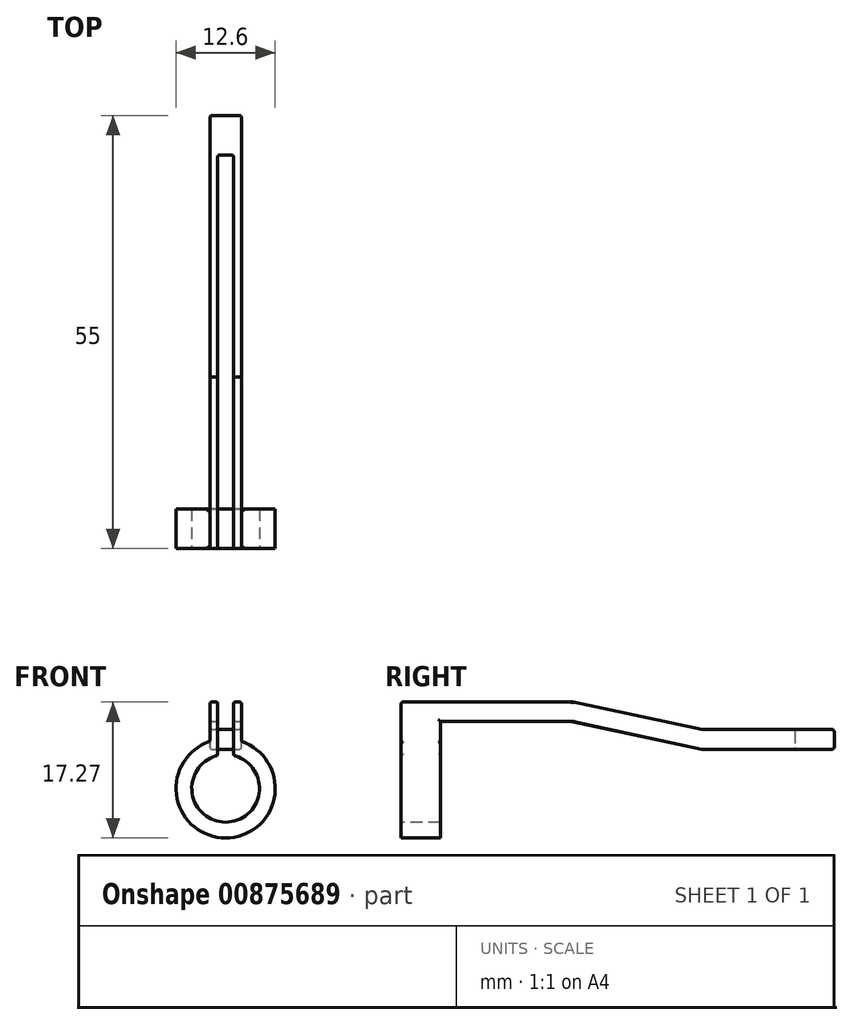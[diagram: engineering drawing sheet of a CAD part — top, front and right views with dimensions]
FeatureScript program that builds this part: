
annotation { "Feature Type Name" : "Feature", "Feature Type Description" : "" }
export const myFeature = defineFeature(function(context is Context, id is Id, definition is map)
    precondition{}
    {
        {
            var Q0;
            Q0=qCreatedBy(makeId("Front.planeOp"),FACE);
            var sketch = newSketch(context, id + "F0", { "sketchPlane" : qUnion([Q0])});
            skCircle(sketch, "E0", {"center": v(0, 0) * mm, "radius": 6.3 * mm});
            skSolve(sketch);
        }
        {
            var Q0;
            Q0 = qSketchRegion(id + "F0", true);
            extrude(context, id + "F1", {"entities" : qUnion([Q0]), "depth" : 5 * mm, "offsetDistance" : 25 * mm});
        }
        {
            var Q0;
            Q0=makeQuery(id+"F1.opExtrude","CAP_FACE",FACE,{"disambiguationData":[OSD([sQuery(id+"F0.wireOp",EDGE,"E0")])],"isStart":false});
            var sketch = newSketch(context, id + "F2", { "sketchPlane" : qUnion([Q0])});
            skCircle(sketch, "E1", {"center": v(0, 0) * mm, "radius": 4.3 * mm});
            skSolve(sketch);
        }
        {
            var Q0;
            Q0=makeQuery(id+"F2.imprint","IMPRINT",FACE,{"disambiguationData":[TD([[makeQuery(id+"F2.imprint","IMPRINT",EDGE,{"derivedFrom":sQuery(id+"F2.wireOp",EDGE,"E1")}),1.0]])]});
            extrude(context, id + "F3", {"entities" : qUnion([Q0]), "operationType" : NewBodyOperationType.REMOVE, "endBound" : BoundingType.UP_TO_NEXT, "oppositeDirection" : true, "depth" : 25 * mm, "offsetDistance" : 25 * mm});
        }
        {
            var Q0;
            Q0=makeQuery(id+"F1.opExtrude","CAP_FACE",FACE,{"disambiguationData":[OSD([sQuery(id+"F0.wireOp",EDGE,"E0")])],"isStart":false});
            var sketch = newSketch(context, id + "F4", { "sketchPlane" : qUnion([Q0])});
            skLineSegment(sketch, "E2.bottom", {"start": v(2, 5.97) * mm, "end": v(-2, 5.97) * mm});
            skLineSegment(sketch, "E2.top", {"start": v(2, 10.97) * mm, "end": v(-2, 10.97) * mm});
            skLineSegment(sketch, "E2.left", {"start": v(2, 5.97) * mm, "end": v(2, 10.97) * mm});
            skLineSegment(sketch, "E2.right", {"start": v(-2, 5.97) * mm, "end": v(-2, 10.97) * mm});
            skPoint(sketch, "E2.middle", {"position": v(0, 8.47) * mm});
            skSolve(sketch);
        }
        {
            var Q0;
            Q0 = qSketchRegion(id + "F4", true);
            extrude(context, id + "F5", {"entities" : qUnion([Q0]), "operationType" : NewBodyOperationType.ADD, "oppositeDirection" : true, "depth" : 5 * mm, "offsetDistance" : 25 * mm});
        }
        {
            var Q0;
            Q0=makeQuery(id+"F5.opExtrude","SWEPT_FACE",FACE,{"disambiguationData":[OSD([sQuery(id+"F4.wireOp",EDGE,"E2.left")])]});
            var sketch = newSketch(context, id + "F6", { "sketchPlane" : qUnion([Q0])});
            skLineSegment(sketch, "E3", {"start": v(0, 10.97) * mm, "end": v(16.79, 10.97) * mm});
            skLineSegment(sketch, "E4", {"start": v(33.21, 7.47) * mm, "end": v(16.79, 10.97) * mm});
            skLineSegment(sketch, "E5", {"start": v(50, 7.47) * mm, "end": v(33.21, 7.47) * mm});
            skLineSegment(sketch, "E6", {"start": v(50, 7.47) * mm, "end": v(50, 4.97) * mm});
            skLineSegment(sketch, "E7", {"start": v(50, 4.97) * mm, "end": v(33.21, 4.97) * mm});
            skLineSegment(sketch, "E8", {"start": v(33.21, 4.97) * mm, "end": v(16.79, 8.47) * mm});
            skLineSegment(sketch, "E9", {"start": v(16.79, 8.47) * mm, "end": v(0, 8.47) * mm});
            skSolve(sketch);
        }
        {
            var Q0;
            {var subQ0=sQuery(id+"F6.wireOp",EDGE,"E3");Q0=makeQuery(id+"F6.imprint","IMPRINT",FACE,{"disambiguationData":[TD([[makeQuery(id+"F6.imprint","IMPRINT",EDGE,{"derivedFrom":subQ0}),-1.0]])]});}
            var Q1;
            Q1=makeQuery(id+"F5.opExtrude","SWEPT_FACE",FACE,{"disambiguationData":[OSD([sQuery(id+"F4.wireOp",EDGE,"E2.right")])]});
            extrude(context, id + "F7", {"entities" : qUnion([Q0]), "operationType" : NewBodyOperationType.ADD, "endBound" : BoundingType.UP_TO_SURFACE, "oppositeDirection" : true, "depth" : 25 * mm, "endBoundEntityFace" : qUnion([Q1]), "offsetDistance" : 25 * mm});
        }
        {
            var Q0;
            Q0=makeQuery(id+"F5.boolean.opBoolean","MERGE",FACE,{"derivedFrom":[makeQuery(id+"F1.opExtrude","CAP_FACE",FACE,{"disambiguationData":[OSD([sQuery(id+"F0.wireOp",EDGE,"E0")])],"isStart":false}),makeQuery(id+"F5.opExtrude","CAP_FACE",FACE,{"disambiguationData":[OSD([sQuery(id+"F4.wireOp",EDGE,"E2.bottom"),sQuery(id+"F4.wireOp",EDGE,"E2.top"),sQuery(id+"F4.wireOp",EDGE,"E2.left"),sQuery(id+"F4.wireOp",EDGE,"E2.right")])],"isStart":true})]});
            var sketch = newSketch(context, id + "F8", { "sketchPlane" : qUnion([Q0])});
            skLineSegment(sketch, "E10.bottom", {"start": v(1, 10.97) * mm, "end": v(-1, 10.97) * mm});
            skLineSegment(sketch, "E10.top", {"start": v(1, 2.97) * mm, "end": v(-1, 2.97) * mm});
            skLineSegment(sketch, "E10.left", {"start": v(1, 10.97) * mm, "end": v(1, 2.97) * mm});
            skLineSegment(sketch, "E10.right", {"start": v(-1, 10.97) * mm, "end": v(-1, 2.97) * mm});
            skPoint(sketch, "E11", {"position": v(0, 2.97) * mm});
            skSolve(sketch);
        }
        {
            var Q0;
            {var subQ0=sQuery(id+"F8.wireOp",EDGE,"E10.bottom");Q0=makeQuery(id+"F8.imprint","IMPRINT",FACE,{"disambiguationData":[TD([[makeQuery(id+"F8.imprint","IMPRINT",EDGE,{"derivedFrom":subQ0}),1.0]])]});}
            var Q1;
            Q1=sQuery(id+"F8.wireOp",EDGE,"E10.right");
            extrude(context, id + "F9", {"entities" : qUnion([Q0]), "operationType" : NewBodyOperationType.REMOVE, "surfaceEntities" : qUnion([Q1]), "oppositeDirection" : true, "depth" : 50 * mm, "offsetDistance" : 25 * mm});
        }
        {
            var Q0;
            Q0=makeQuery(id+"F7.opExtrude","CAP_EDGE",EDGE,{"disambiguationData":[OSD([sQuery(id+"F6.wireOp",EDGE,"E9")])],"isStart":false});
            var Q1;
            Q1=makeQuery(id+"F5.opExtrude","CAP_EDGE",EDGE,{"disambiguationData":[OSD([sQuery(id+"F4.wireOp",EDGE,"E2.right")])],"isStart":false});
            var Q2;
            Q2=makeQuery(id+"F9.boolean.opBoolean","INTERSECT",EDGE,{"derivedFrom":[makeQuery(id+"F5.boolean.opBoolean","MERGE",FACE,{"derivedFrom":[makeQuery(id+"F1.opExtrude","CAP_FACE",FACE,{"disambiguationData":[OSD([sQuery(id+"F0.wireOp",EDGE,"E0")])],"isStart":true}),makeQuery(id+"F5.opExtrude","CAP_FACE",FACE,{"disambiguationData":[OSD([sQuery(id+"F4.wireOp",EDGE,"E2.bottom"),sQuery(id+"F4.wireOp",EDGE,"E2.top"),sQuery(id+"F4.wireOp",EDGE,"E2.left"),sQuery(id+"F4.wireOp",EDGE,"E2.right")])],"isStart":false})]}),makeQuery(id+"F9.opExtrude","SWEPT_FACE",FACE,{"disambiguationData":[OSD([sQuery(id+"F8.wireOp",EDGE,"E10.right")])]})]});
            var Q3;
            {var subQ0=sQuery(id+"F6.wireOp",EDGE,"E9");var subQ1=sQuery(id+"F4.wireOp",EDGE,"E2.left");var subQ2=sQuery(id+"F4.wireOp",EDGE,"E2.right");Q3=makeQuery(id+"F9.boolean.opBoolean","SPLIT",EDGE,{"disambiguationData":[TD([makeQuery(id+"F5.opExtrude","SWEPT_FACE",FACE,{"disambiguationData":[OSD([subQ2])]})])],"derivedFrom":makeQuery(id+"F7.opExtrude","SWEPT_EDGE",EDGE,{"disambiguationData":[OSD([subQ1,subQ0])]})});}
            var Q4;
            Q4=makeQuery(id+"F9.boolean.opBoolean","INTERSECT",EDGE,{"derivedFrom":[makeQuery(id+"F7.opExtrude","SWEPT_FACE",FACE,{"disambiguationData":[OSD([sQuery(id+"F6.wireOp",EDGE,"E9")])]}),makeQuery(id+"F9.opExtrude","SWEPT_FACE",FACE,{"disambiguationData":[OSD([sQuery(id+"F8.wireOp",EDGE,"E10.right")])]})]});
            var Q5;
            {var subQ0=sQuery(id+"F6.wireOp",EDGE,"E9");var subQ1=sQuery(id+"F6.wireOp",EDGE,"E8");Q5=makeQuery(id+"F9.boolean.opBoolean","SPLIT",EDGE,{"disambiguationData":[TD([makeQuery(id+"F5.opExtrude","SWEPT_FACE",FACE,{"disambiguationData":[OSD([sQuery(id+"F4.wireOp",EDGE,"E2.right")])]})])],"derivedFrom":makeQuery(id+"F7.opExtrude","SWEPT_EDGE",EDGE,{"disambiguationData":[OSD([subQ1,subQ0])]})});}
            var Q6;
            Q6=makeQuery(id+"F7.boolean.opBoolean","MERGE",FACE,{"derivedFrom":[makeQuery(id+"F5.opExtrude","SWEPT_FACE",FACE,{"disambiguationData":[OSD([sQuery(id+"F4.wireOp",EDGE,"E2.right")])]}),makeQuery(id+"F7.opExtrude","CAP_FACE",FACE,{"disambiguationData":[OSD([sQuery(id+"F4.wireOp",EDGE,"E2.left"),sQuery(id+"F6.wireOp",EDGE,"E3"),sQuery(id+"F6.wireOp",EDGE,"E4"),sQuery(id+"F6.wireOp",EDGE,"E5"),sQuery(id+"F6.wireOp",EDGE,"E6"),sQuery(id+"F6.wireOp",EDGE,"E7"),sQuery(id+"F6.wireOp",EDGE,"E8"),sQuery(id+"F6.wireOp",EDGE,"E9")])],"isStart":false})]});
            var Q7;
            Q7=makeQuery(id+"F9.boolean.opBoolean","INTERSECT",EDGE,{"derivedFrom":[makeQuery(id+"F7.opExtrude","SWEPT_FACE",FACE,{"disambiguationData":[OSD([sQuery(id+"F6.wireOp",EDGE,"E8")])]}),makeQuery(id+"F9.opExtrude","SWEPT_FACE",FACE,{"disambiguationData":[OSD([sQuery(id+"F8.wireOp",EDGE,"E10.right")])]})]});
            var Q8;
            {var subQ0=sQuery(id+"F6.wireOp",EDGE,"E8");var subQ1=sQuery(id+"F6.wireOp",EDGE,"E7");Q8=makeQuery(id+"F9.boolean.opBoolean","SPLIT",EDGE,{"disambiguationData":[TD([makeQuery(id+"F5.opExtrude","SWEPT_FACE",FACE,{"disambiguationData":[OSD([sQuery(id+"F4.wireOp",EDGE,"E2.right")])]})])],"derivedFrom":makeQuery(id+"F7.opExtrude","SWEPT_EDGE",EDGE,{"disambiguationData":[OSD([subQ1,subQ0])]})});}
            var Q9;
            Q9=makeQuery(id+"F9.boolean.opBoolean","COPY",FACE,{"derivedFrom":makeQuery(id+"F9.opExtrude","SWEPT_FACE",FACE,{"disambiguationData":[OSD([sQuery(id+"F8.wireOp",EDGE,"E10.right")])]})});
            var Q10;
            Q10=makeQuery(id+"F9.boolean.opBoolean","COPY",FACE,{"derivedFrom":makeQuery(id+"F9.opExtrude","SWEPT_FACE",FACE,{"disambiguationData":[OSD([sQuery(id+"F8.wireOp",EDGE,"E10.left")])]})});
            var Q11;
            Q11=makeQuery(id+"F7.opExtrude","SWEPT_FACE",FACE,{"disambiguationData":[OSD([sQuery(id+"F6.wireOp",EDGE,"E7")])]});
            var Q12;
            {var subQ0=sQuery(id+"F4.wireOp",EDGE,"E2.left");Q12=makeQuery(id+"F7.boolean.opBoolean","MERGE",FACE,{"derivedFrom":[makeQuery(id+"F5.opExtrude","SWEPT_FACE",FACE,{"disambiguationData":[OSD([subQ0])]}),makeQuery(id+"F7.opExtrude","CAP_FACE",FACE,{"disambiguationData":[OSD([subQ0,sQuery(id+"F6.wireOp",EDGE,"E3"),sQuery(id+"F6.wireOp",EDGE,"E4"),sQuery(id+"F6.wireOp",EDGE,"E5"),sQuery(id+"F6.wireOp",EDGE,"E6"),sQuery(id+"F6.wireOp",EDGE,"E7"),sQuery(id+"F6.wireOp",EDGE,"E8"),sQuery(id+"F6.wireOp",EDGE,"E9")])],"isStart":true})]});}
            var Q13;
            Q13=makeQuery(id+"F7.opExtrude","SWEPT_FACE",FACE,{"disambiguationData":[OSD([sQuery(id+"F6.wireOp",EDGE,"E5")])]});
            fillet(context, id + "F10", {"entities" : qUnion([Q0, Q1, Q2, Q3, Q4, Q5, Q6, Q7, Q8, Q9, Q10, Q11, Q12, Q13]), "radius" : 0.25 * mm, "tangentPropagation" : true, "allowEdgeOverflow" : false});
        }
        {
            var Q0;
            {var subQ0=sQuery(id+"F4.wireOp",EDGE,"E2.left");var subQ1=sQuery(id+"F4.wireOp",EDGE,"E2.top");Q0=makeQuery(id+"F9.boolean.opBoolean","SPLIT",EDGE,{"disambiguationData":[TD([makeQuery(id+"F5.opExtrude","SWEPT_FACE",FACE,{"disambiguationData":[OSD([subQ0])]})])],"derivedFrom":makeQuery(id+"F5.opExtrude","CAP_EDGE",EDGE,{"disambiguationData":[OSD([subQ1])],"isStart":true})});}
            var Q1;
            {var subQ0=sQuery(id+"F4.wireOp",EDGE,"E2.top");var subQ1=sQuery(id+"F4.wireOp",EDGE,"E2.right");Q1=makeQuery(id+"F9.boolean.opBoolean","SPLIT",EDGE,{"disambiguationData":[TD([makeQuery(id+"F5.opExtrude","SWEPT_FACE",FACE,{"disambiguationData":[OSD([subQ1])]})])],"derivedFrom":makeQuery(id+"F5.opExtrude","CAP_EDGE",EDGE,{"disambiguationData":[OSD([subQ0])],"isStart":true})});}
            fillet(context, id + "F11", {"entities" : qUnion([Q0, Q1]), "radius" : 0.25 * mm, "tangentPropagation" : true, "allowEdgeOverflow" : false});
        }
    });
